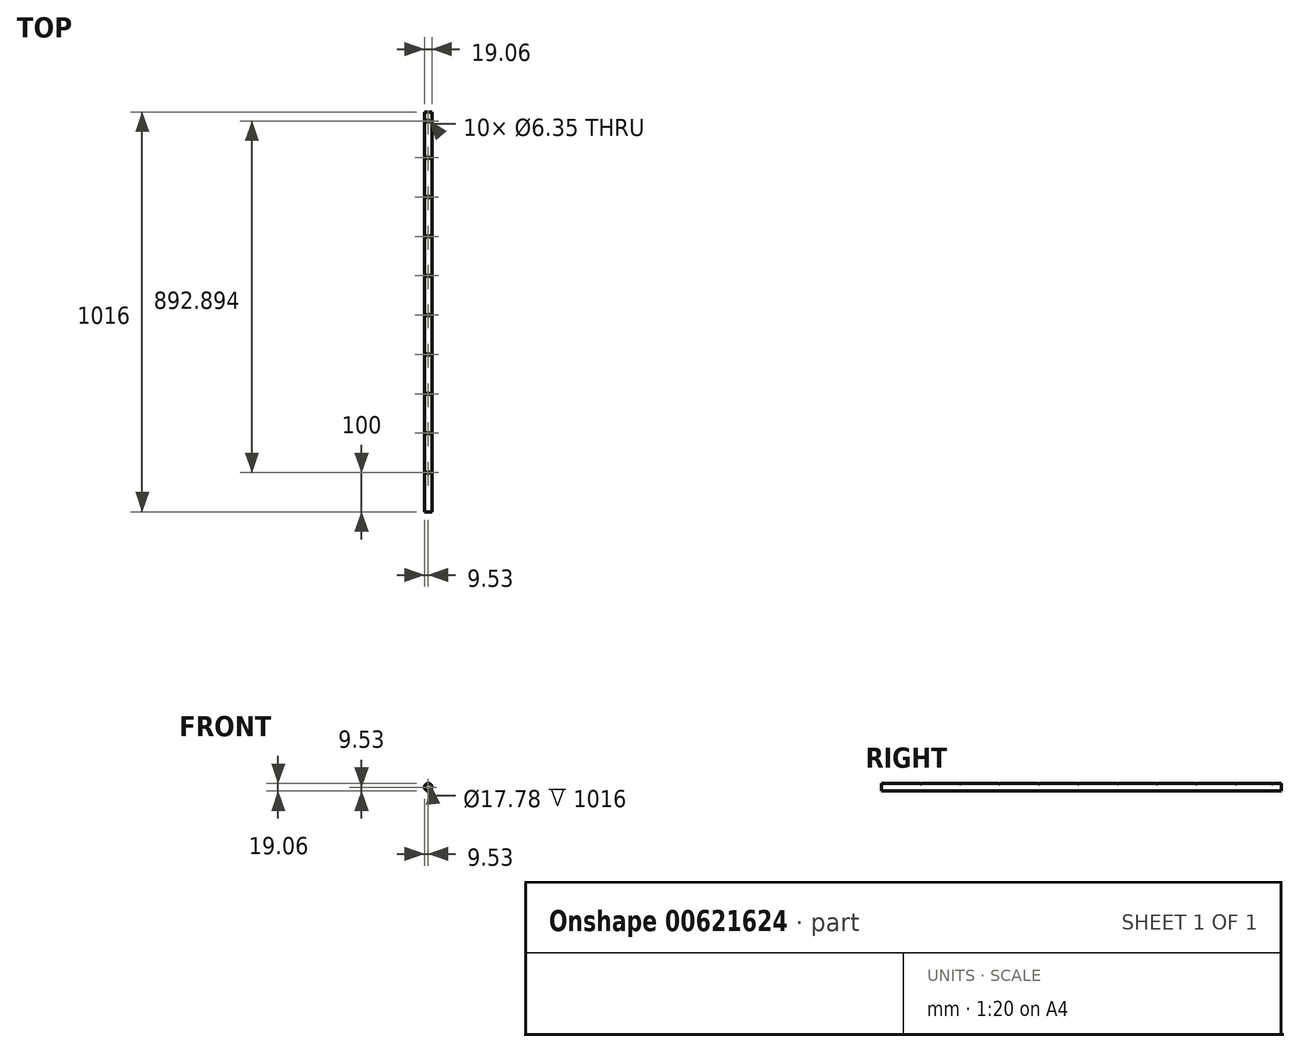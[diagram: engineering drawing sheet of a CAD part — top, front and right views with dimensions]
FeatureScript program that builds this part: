
annotation { "Feature Type Name" : "Feature", "Feature Type Description" : "" }
export const myFeature = defineFeature(function(context is Context, id is Id, definition is map)
    precondition{}
    {
        {
            var Q0;
            Q0=qCreatedBy(makeId("Front.planeOp"),FACE);
            var sketch = newSketch(context, id + "F0", { "sketchPlane" : qUnion([Q0])});
            skCircle(sketch, "E0", {"center": v(0, 0) * mm, "radius": 9.53 * mm});
            skSolve(sketch);
        }
        {
            var Q0;
            Q0=makeQuery(id+"F0.imprint","IMPRINT",FACE,{"disambiguationData":[TD([[makeQuery(id+"F0.imprint","IMPRINT",EDGE,{"derivedFrom":sQuery(id+"F0.wireOp",EDGE,"E0")}),1.0]])]});
            extrude(context, id + "F1", {"entities" : qUnion([Q0]), "oppositeDirection" : true, "depth" : 1016 * mm, "offsetDistance" : 25.4 * mm});
        }
        {
            var Q0;
            Q0=qCreatedBy(makeId("Front.planeOp"),FACE);
            var sketch = newSketch(context, id + "F2", { "sketchPlane" : qUnion([Q0])});
            skCircle(sketch, "E1", {"center": v(0, 0) * mm, "radius": 8.9 * mm});
            skSolve(sketch);
        }
        {
            var Q0;
            Q0 = qSketchRegion(id + "F2", true);
            extrude(context, id + "F3", {"entities" : qUnion([Q0]), "operationType" : NewBodyOperationType.REMOVE, "oppositeDirection" : true, "depth" : 1016 * mm, "offsetDistance" : 25.4 * mm});
        }
        {
            var Q0;
            Q0=qCreatedBy(makeId("Top.planeOp"),FACE);
            cPlane(context, id + "F4", {"entities" : qUnion([Q0]), "cplaneType" : CPlaneType.OFFSET, "offset" : 9.52 * mm, "width" : 152.4 * mm, "height" : 152.4 * mm});
        }
        {
            var Q0;
            Q0=qCreatedBy(id+"F4.planeOp",FACE);
            var sketch = newSketch(context, id + "F5", { "sketchPlane" : qUnion([Q0])});
            skPoint(sketch, "E2", {"position": v(0, 200) * mm});
            skPoint(sketch, "E3", {"position": v(0, 300) * mm});
            skPoint(sketch, "E4", {"position": v(0, 400) * mm});
            skPoint(sketch, "E5", {"position": v(0, 500) * mm});
            skPoint(sketch, "E6", {"position": v(0, 600) * mm});
            skPoint(sketch, "E7", {"position": v(0, 700) * mm});
            skPoint(sketch, "E8", {"position": v(0, 800) * mm});
            skPoint(sketch, "E9", {"position": v(0, 900) * mm});
            skPoint(sketch, "E10", {"position": v(0, 992.9) * mm});
            skPoint(sketch, "E11", {"position": v(0, 100) * mm});
            skSolve(sketch);
        }
        {
            var Q0;
            Q0=sQuery(id+"F5.wireOp",VERTEX,"E2");
            var Q1;
            Q1=sQuery(id+"F5.wireOp",VERTEX,"E3");
            var Q2;
            Q2=sQuery(id+"F5.wireOp",VERTEX,"E4");
            var Q3;
            Q3=sQuery(id+"F5.wireOp",VERTEX,"E5");
            var Q4;
            Q4=sQuery(id+"F5.wireOp",VERTEX,"E6");
            var Q5;
            Q5=sQuery(id+"F5.wireOp",VERTEX,"E7");
            var Q6;
            Q6=sQuery(id+"F5.wireOp",VERTEX,"E8");
            var Q7;
            Q7=sQuery(id+"F5.wireOp",VERTEX,"E9");
            var Q8;
            Q8=sQuery(id+"F5.wireOp",VERTEX,"E10");
            var Q9;
            Q9=sQuery(id+"F5.wireOp",VERTEX,"E11");
            var Q10;
            Q10=makeQuery(id+"F1.opExtrude","SWEPT_BODY",BODY,{"disambiguationData":[OSD([sQuery(id+"F0.wireOp",EDGE,"E0")])]});
            hole(context, id + "F6", {"style" : HoleStyle.SIMPLE, "endStyle" : HoleEndStyle.BLIND, "holeDiameter" : 6.35 * mm, "majorDiameter" : 6.35 * mm, "holeDepth" : 12.7 * mm, "isTappedThrough" : true, "tappedDepth" : 12.7 * mm, "tapClearance" : 3, "locations" : qUnion([Q0, Q1, Q2, Q3, Q4, Q5, Q6, Q7, Q8, Q9]), "scope" : qUnion([Q10])});
        }
    });
